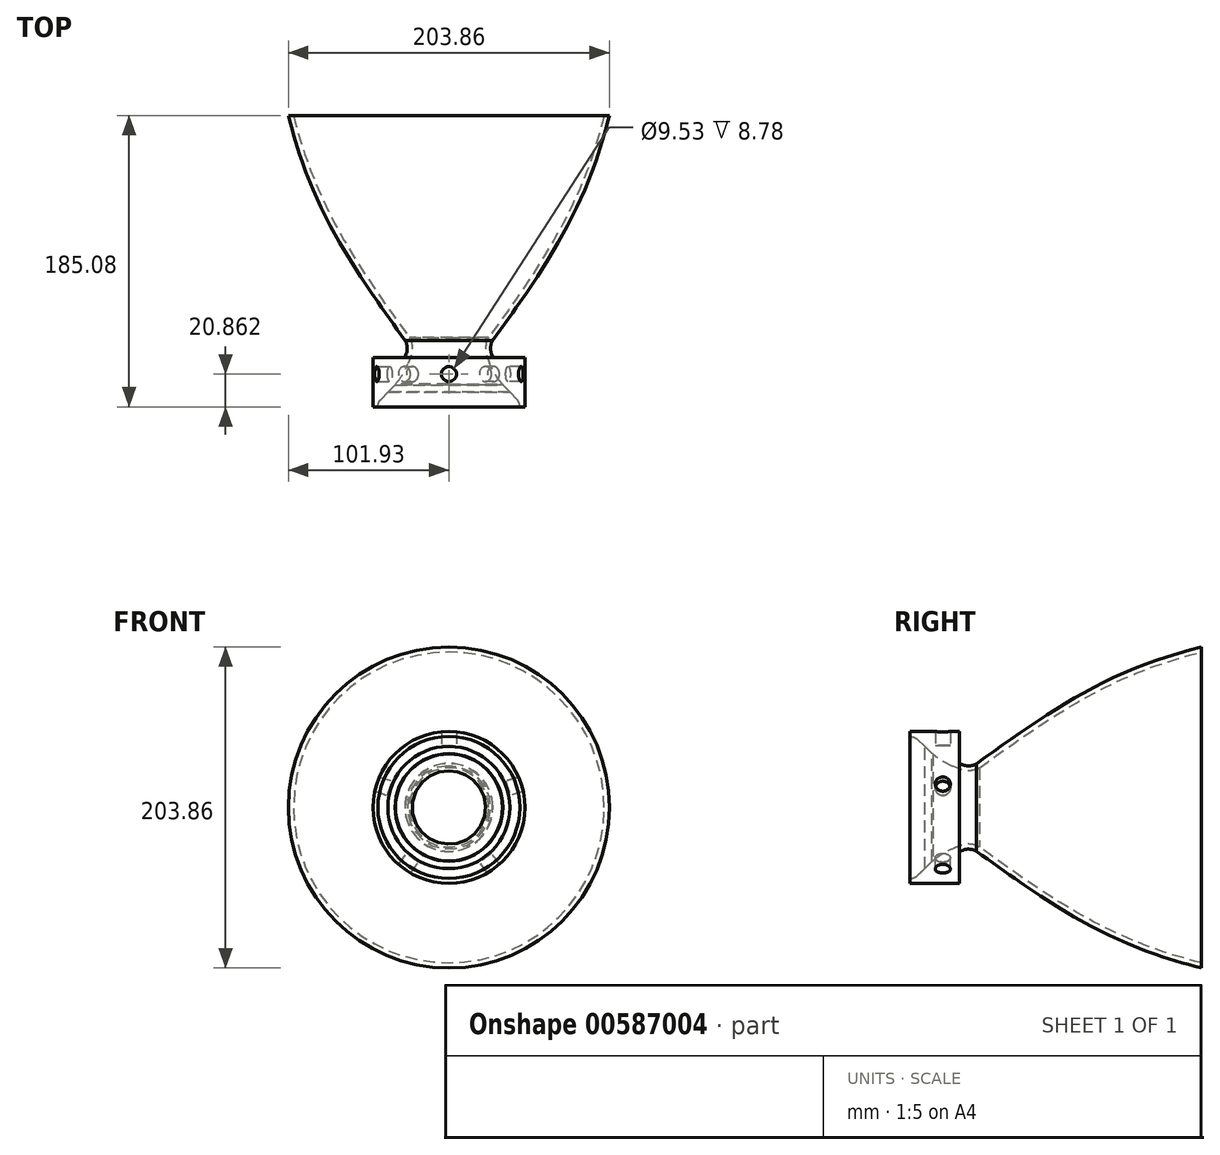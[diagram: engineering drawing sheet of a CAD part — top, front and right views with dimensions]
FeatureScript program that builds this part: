
annotation { "Feature Type Name" : "Feature", "Feature Type Description" : "" }
export const myFeature = defineFeature(function(context is Context, id is Id, definition is map)
    precondition{}
    {
        {
            var Q0;
            Q0=qCreatedBy(makeId("Right.planeOp"),FACE);
            var sketch = newSketch(context, id + "F0", { "sketchPlane" : qUnion([Q0])});
            skPoint(sketch, "E0", {"position": v(0, 25.4) * mm});
            skLineSegment(sketch, "E1", {"start": v(303.28, 127) * mm, "end": v(303.28, 0) * mm});
            skLineSegment(sketch, "E2", {"start": v(303.28, 0) * mm, "end": v(0, 0) * mm});
            skLineSegment(sketch, "E3", {"start": v(-31.1, 45.47) * mm, "end": v(-22.09, 36.92) * mm});
            skLineSegment(sketch, "E4", {"start": v(-9.32, 28.91) * mm, "end": v(-4.5, 27.1) * mm});
            skArc(sketch, "E5.filletArc", {"start": v(-4.5, 27.1) * mm, "mid": v(-0.09, 26.48) * mm, "end": v(4.17, 27.8) * mm});
            skPoint(sketch, "E6.visualSharp", {"position": v(-16.51, 31.63) * mm});
            skArc(sketch, "E6.filletArc", {"start": v(-22.09, 36.92) * mm, "mid": v(-16.1, 32.28) * mm, "end": v(-9.32, 28.91) * mm});
            skPoint(sketch, "E7.visualSharp", {"position": v(-34.05, 48.26) * mm});
            skArc(sketch, "E7.filletArc", {"start": v(-31.1, 45.47) * mm, "mid": v(-34.34, 47.54) * mm, "end": v(-38.1, 48.26) * mm});
            skFitSpline(sketch, "E8", {"points": [v(4.17, 27.8) * mm, v(117.26, 93.1) * mm, v(252.98, 119.48) * mm, v(303.28, 127) * mm], "startDerivative": vector(275.36, 198.38) * mm, "endDerivative": vector(183.33, 30.03) * mm});
            skLineSegment(sketch, "E9", {"start": v(-38.1, 48.26) * mm, "end": v(-38.1, 0) * mm});
            skLineSegment(sketch, "E10", {"start": v(-38.1, 0) * mm, "end": v(0, 0) * mm});
            skSolve(sketch);
        }
        {
            var Q0;
            Q0 = qSketchRegion(id + "F0", true);
            var Q1;
            Q1=sQuery(id+"F0.wireOp",EDGE,"E2");
            revolve(context, id + "F1", {"entities" : qUnion([Q0]), "axis" : qUnion([Q1]), "revolveType" : RevolveType.FULL});
        }
        {
            var Q0;
            Q0=makeQuery(id+"F1.opRevolve","SWEPT_FACE",FACE,{"disambiguationData":[OSD([sQuery(id+"F0.wireOp",EDGE,"E9")])]});
            cPlane(context, id + "F2", {"entities" : qUnion([Q0]), "cplaneType" : CPlaneType.OFFSET, "offset" : 27.18 * mm, "oppositeDirection" : true, "width" : 152.4 * mm, "height" : 152.4 * mm});
        }
        {
            var Q0;
            Q0=qCreatedBy(id+"F2.planeOp",FACE);
            var sketch = newSketch(context, id + "F3", { "sketchPlane" : qUnion([Q0])});
            skLineSegment(sketch, "E11.bottom", {"start": v(0, 61.38) * mm, "end": v(4.76, 61.38) * mm});
            skLineSegment(sketch, "E11.top", {"start": v(0, 33.85) * mm, "end": v(4.76, 33.85) * mm});
            skLineSegment(sketch, "E11.left", {"start": v(0, 61.38) * mm, "end": v(0, 33.85) * mm});
            skLineSegment(sketch, "E11.right", {"start": v(4.76, 61.38) * mm, "end": v(4.76, 33.85) * mm});
            skLineSegment(sketch, "E12.1.0", {"start": v(-58.37, 18.97) * mm, "end": v(-32.2, 10.46) * mm});
            skLineSegment(sketch, "E12.1.1", {"start": v(-56.9, 23.5) * mm, "end": v(-30.72, 15) * mm});
            skLineSegment(sketch, "E12.1.2", {"start": v(-58.37, 18.97) * mm, "end": v(-56.9, 23.5) * mm});
            skLineSegment(sketch, "E12.1.3", {"start": v(-32.2, 10.46) * mm, "end": v(-30.72, 15) * mm});
            skLineSegment(sketch, "E12.2.0", {"start": v(-36.08, -49.65) * mm, "end": v(-19.9, -27.39) * mm});
            skLineSegment(sketch, "E12.2.1", {"start": v(-39.93, -46.85) * mm, "end": v(-23.75, -24.59) * mm});
            skLineSegment(sketch, "E12.2.2", {"start": v(-36.08, -49.65) * mm, "end": v(-39.93, -46.85) * mm});
            skLineSegment(sketch, "E12.2.3", {"start": v(-19.9, -27.39) * mm, "end": v(-23.75, -24.59) * mm});
            skLineSegment(sketch, "E12.3.0", {"start": v(36.08, -49.65) * mm, "end": v(19.9, -27.39) * mm});
            skLineSegment(sketch, "E12.3.1", {"start": v(32.22, -52.45) * mm, "end": v(16.05, -30.19) * mm});
            skLineSegment(sketch, "E12.3.2", {"start": v(36.08, -49.65) * mm, "end": v(32.22, -52.45) * mm});
            skLineSegment(sketch, "E12.3.3", {"start": v(19.9, -27.39) * mm, "end": v(16.05, -30.19) * mm});
            skLineSegment(sketch, "E12.4.0", {"start": v(58.37, 18.97) * mm, "end": v(32.2, 10.46) * mm});
            skLineSegment(sketch, "E12.4.1", {"start": v(59.84, 14.44) * mm, "end": v(33.67, 5.93) * mm});
            skLineSegment(sketch, "E12.4.2", {"start": v(58.37, 18.97) * mm, "end": v(59.84, 14.44) * mm});
            skLineSegment(sketch, "E12.4.3", {"start": v(32.2, 10.46) * mm, "end": v(33.67, 5.93) * mm});
            skPoint(sketch, "E12.center", {"position": v(0, 0) * mm});
            skSolve(sketch);
        }
        {
            var Q0;
            Q0=makeQuery(id+"F3.imprint","IMPRINT",FACE,{"disambiguationData":[TD([[makeQuery(id+"F3.imprint","IMPRINT",EDGE,{"derivedFrom":sQuery(id+"F3.wireOp",EDGE,"E11.bottom")}),-1.0]])]});
            var Q1;
            Q1=sQuery(id+"F3.wireOp",EDGE,"E11.left");
            revolve(context, id + "F4", {"operationType" : NewBodyOperationType.REMOVE, "entities" : qUnion([Q0]), "axis" : qUnion([Q1]), "revolveType" : RevolveType.FULL, "oppositeDirection" : true});
        }
        {
            var Q0;
            Q0=makeQuery(id+"F3.imprint","IMPRINT",FACE,{"disambiguationData":[TD([[makeQuery(id+"F3.imprint","IMPRINT",EDGE,{"derivedFrom":sQuery(id+"F3.wireOp",EDGE,"E12.4.0")}),1.0]])]});
            var Q1;
            Q1=sQuery(id+"F3.wireOp",EDGE,"E12.4.0");
            revolve(context, id + "F5", {"operationType" : NewBodyOperationType.REMOVE, "entities" : qUnion([Q0]), "axis" : qUnion([Q1]), "revolveType" : RevolveType.FULL, "oppositeDirection" : true});
        }
        {
            var Q0;
            Q0=makeQuery(id+"F3.imprint","IMPRINT",FACE,{"disambiguationData":[TD([[makeQuery(id+"F3.imprint","IMPRINT",EDGE,{"derivedFrom":sQuery(id+"F3.wireOp",EDGE,"E12.3.0")}),1.0]])]});
            var Q1;
            Q1=sQuery(id+"F3.wireOp",EDGE,"E12.3.0");
            revolve(context, id + "F6", {"operationType" : NewBodyOperationType.REMOVE, "entities" : qUnion([Q0]), "axis" : qUnion([Q1]), "revolveType" : RevolveType.FULL});
        }
        {
            var Q0;
            Q0=makeQuery(id+"F3.imprint","IMPRINT",FACE,{"disambiguationData":[TD([[makeQuery(id+"F3.imprint","IMPRINT",EDGE,{"derivedFrom":sQuery(id+"F3.wireOp",EDGE,"E12.2.0")}),1.0]])]});
            var Q1;
            Q1=sQuery(id+"F3.wireOp",EDGE,"E12.2.0");
            revolve(context, id + "F7", {"operationType" : NewBodyOperationType.REMOVE, "entities" : qUnion([Q0]), "axis" : qUnion([Q1]), "revolveType" : RevolveType.FULL, "oppositeDirection" : true});
        }
        {
            var Q0;
            Q0=makeQuery(id+"F3.imprint","IMPRINT",FACE,{"disambiguationData":[TD([[makeQuery(id+"F3.imprint","IMPRINT",EDGE,{"derivedFrom":sQuery(id+"F3.wireOp",EDGE,"E12.1.0")}),1.0]])]});
            var Q1;
            Q1=sQuery(id+"F3.wireOp",EDGE,"E12.1.0");
            revolve(context, id + "F8", {"operationType" : NewBodyOperationType.REMOVE, "entities" : qUnion([Q0]), "axis" : qUnion([Q1]), "revolveType" : RevolveType.FULL});
        }
        {
            var Q0;
            Q0=makeQuery(id+"F1.opRevolve","SWEPT_FACE",FACE,{"disambiguationData":[OSD([sQuery(id+"F0.wireOp",EDGE,"E1")])]});
            var Q1;
            Q1=makeQuery(id+"F1.opRevolve","SWEPT_FACE",FACE,{"disambiguationData":[OSD([sQuery(id+"F0.wireOp",EDGE,"Ow1FXaBQ-uKWU-AUm1-Qf29-WGxy1pBPwJRH")])]});
            var Q2;
            Q2=makeQuery(id+"F1.opRevolve","SWEPT_FACE",FACE,{"disambiguationData":[OSD([sQuery(id+"F0.wireOp",EDGE,"E9")])]});
            shell(context, id + "F9", {"entities" : qUnion([Q0, Q1, Q2]), "thickness" : 3.17 * mm});
        }
        {
            var Q0;
            Q0=qCreatedBy(makeId("Right.planeOp"),FACE);
            var sketch = newSketch(context, id + "F10", { "sketchPlane" : qUnion([Q0])});
            skLineSegment(sketch, "E13.bottom", {"start": v(-146.71, 202.99) * mm, "end": v(438.5, 202.99) * mm});
            skLineSegment(sketch, "E13.top", {"start": v(-146.71, -194.5) * mm, "end": v(438.5, -194.5) * mm});
            skLineSegment(sketch, "E13.left", {"start": v(-146.71, 202.99) * mm, "end": v(-146.71, -194.5) * mm});
            skLineSegment(sketch, "E13.right", {"start": v(438.5, 202.99) * mm, "end": v(438.5, -194.5) * mm});
            skSolve(sketch);
        }
        {
            var Q0;
            Q0=qCreatedBy(makeId("Right.planeOp"),FACE);
            var sketch = newSketch(context, id + "F11", { "sketchPlane" : qUnion([Q0])});
            skArc(sketch, "E14.0", {"start": v(-38.1, 48.26) * mm, "mid": v(-34.34, 47.54) * mm, "end": v(-31.1, 45.47) * mm, "construction": true});
            skLineSegment(sketch, "E15", {"start": v(-38.1, 48.26) * mm, "end": v(-6.82, 48.26) * mm});
            skLineSegment(sketch, "E16", {"start": v(-6.82, 48.26) * mm, "end": v(-6.82, 26.64) * mm});
            skLineSegment(sketch, "E17", {"start": v(-6.82, 26.64) * mm, "end": v(-24.12, 34.21) * mm});
            skLineSegment(sketch, "E18", {"start": v(-24.12, 34.21) * mm, "end": v(-38.1, 48.26) * mm});
            skLineSegment(sketch, "E19", {"start": v(-117.34, 0) * mm, "end": v(111.52, 0) * mm, "construction": true});
            skSolve(sketch);
        }
        {
            var Q0;
            Q0=makeQuery(id+"F11.imprint","IMPRINT",FACE,{"disambiguationData":[TD([[makeQuery(id+"F11.imprint","IMPRINT",EDGE,{"derivedFrom":sQuery(id+"F11.wireOp",EDGE,"E15")}),-1.0]])]});
            var Q1;
            Q1=sQuery(id+"F11.wireOp",EDGE,"E19");
            revolve(context, id + "F12", {"operationType" : NewBodyOperationType.ADD, "entities" : qUnion([Q0]), "axis" : qUnion([Q1]), "revolveType" : RevolveType.FULL});
        }
        {
            var Q0;
            Q0=makeQuery(id+"F12.opRevolve","SWEPT_FACE",FACE,{"disambiguationData":[OSD([sQuery(id+"F11.wireOp",EDGE,"E16")])]});
            cPlane(context, id + "F13", {"entities" : qUnion([Q0]), "cplaneType" : CPlaneType.OFFSET, "offset" : 10.4 * mm, "oppositeDirection" : true, "width" : 152.4 * mm, "height" : 152.4 * mm});
        }
        {
            var Q0;
            Q0=qCreatedBy(id+"F13.planeOp",FACE);
            var sketch = newSketch(context, id + "F14", { "sketchPlane" : qUnion([Q0])});
            skLineSegment(sketch, "E20.bottom", {"start": v(0, 57.26) * mm, "end": v(-4.76, 57.26) * mm});
            skLineSegment(sketch, "E20.top", {"start": v(0, 39.48) * mm, "end": v(-4.76, 39.48) * mm});
            skLineSegment(sketch, "E20.left", {"start": v(0, 57.26) * mm, "end": v(0, 39.48) * mm});
            skLineSegment(sketch, "E20.right", {"start": v(-4.76, 57.26) * mm, "end": v(-4.76, 39.48) * mm});
            skLineSegment(sketch, "E21.1.0", {"start": v(-54.46, 17.7) * mm, "end": v(-37.55, 12.2) * mm});
            skLineSegment(sketch, "E21.1.1", {"start": v(-55.93, 13.17) * mm, "end": v(-39.02, 7.67) * mm});
            skLineSegment(sketch, "E21.1.2", {"start": v(-54.46, 17.7) * mm, "end": v(-55.93, 13.17) * mm});
            skLineSegment(sketch, "E21.1.3", {"start": v(-37.55, 12.2) * mm, "end": v(-39.02, 7.67) * mm});
            skLineSegment(sketch, "E21.2.0", {"start": v(-33.66, -46.33) * mm, "end": v(-23.2, -31.94) * mm});
            skLineSegment(sketch, "E21.2.1", {"start": v(-29.8, -49.12) * mm, "end": v(-19.35, -34.74) * mm});
            skLineSegment(sketch, "E21.2.2", {"start": v(-33.66, -46.33) * mm, "end": v(-29.8, -49.12) * mm});
            skLineSegment(sketch, "E21.2.3", {"start": v(-23.2, -31.94) * mm, "end": v(-19.35, -34.74) * mm});
            skLineSegment(sketch, "E21.3.0", {"start": v(33.66, -46.33) * mm, "end": v(23.2, -31.94) * mm});
            skLineSegment(sketch, "E21.3.1", {"start": v(37.51, -43.53) * mm, "end": v(27.06, -29.14) * mm});
            skLineSegment(sketch, "E21.3.2", {"start": v(33.66, -46.33) * mm, "end": v(37.51, -43.53) * mm});
            skLineSegment(sketch, "E21.3.3", {"start": v(23.2, -31.94) * mm, "end": v(27.06, -29.14) * mm});
            skLineSegment(sketch, "E21.4.0", {"start": v(54.46, 17.7) * mm, "end": v(37.55, 12.2) * mm});
            skLineSegment(sketch, "E21.4.1", {"start": v(52.99, 22.22) * mm, "end": v(36.08, 16.73) * mm});
            skLineSegment(sketch, "E21.4.2", {"start": v(54.46, 17.7) * mm, "end": v(52.99, 22.22) * mm});
            skLineSegment(sketch, "E21.4.3", {"start": v(37.55, 12.2) * mm, "end": v(36.08, 16.73) * mm});
            skPoint(sketch, "E21.center", {"position": v(0, 0) * mm});
            skSolve(sketch);
        }
        {
            var Q0;
            Q0=makeQuery(id+"F14.imprint","IMPRINT",FACE,{"disambiguationData":[TD([[makeQuery(id+"F14.imprint","IMPRINT",EDGE,{"derivedFrom":sQuery(id+"F14.wireOp",EDGE,"E20.bottom")}),1.0]])]});
            var Q1;
            Q1=sQuery(id+"F14.wireOp",EDGE,"E20.left");
            revolve(context, id + "F15", {"operationType" : NewBodyOperationType.REMOVE, "entities" : qUnion([Q0]), "axis" : qUnion([Q1]), "revolveType" : RevolveType.FULL, "oppositeDirection" : true});
        }
        {
            var Q0;
            Q0=makeQuery(id+"F14.imprint","IMPRINT",FACE,{"disambiguationData":[TD([[makeQuery(id+"F14.imprint","IMPRINT",EDGE,{"derivedFrom":sQuery(id+"F14.wireOp",EDGE,"E21.1.0")}),-1.0]])]});
            var Q1;
            Q1=sQuery(id+"F14.wireOp",EDGE,"E21.1.0");
            revolve(context, id + "F16", {"operationType" : NewBodyOperationType.REMOVE, "entities" : qUnion([Q0]), "axis" : qUnion([Q1]), "revolveType" : RevolveType.FULL, "oppositeDirection" : true});
        }
        {
            var Q0;
            Q0=makeQuery(id+"F14.imprint","IMPRINT",FACE,{"disambiguationData":[TD([[makeQuery(id+"F14.imprint","IMPRINT",EDGE,{"derivedFrom":sQuery(id+"F14.wireOp",EDGE,"E21.2.0")}),-1.0]])]});
            var Q1;
            Q1=sQuery(id+"F14.wireOp",EDGE,"E21.2.0");
            revolve(context, id + "F17", {"operationType" : NewBodyOperationType.REMOVE, "entities" : qUnion([Q0]), "axis" : qUnion([Q1]), "revolveType" : RevolveType.FULL, "oppositeDirection" : true});
        }
        {
            var Q0;
            Q0=makeQuery(id+"F14.imprint","IMPRINT",FACE,{"disambiguationData":[TD([[makeQuery(id+"F14.imprint","IMPRINT",EDGE,{"derivedFrom":sQuery(id+"F14.wireOp",EDGE,"E21.4.0")}),-1.0]])]});
            var Q1;
            Q1=sQuery(id+"F14.wireOp",EDGE,"E21.4.0");
            revolve(context, id + "F18", {"operationType" : NewBodyOperationType.REMOVE, "entities" : qUnion([Q0]), "axis" : qUnion([Q1]), "revolveType" : RevolveType.FULL, "oppositeDirection" : true});
        }
        {
            var Q0;
            Q0=makeQuery(id+"F14.imprint","IMPRINT",FACE,{"disambiguationData":[TD([[makeQuery(id+"F14.imprint","IMPRINT",EDGE,{"derivedFrom":sQuery(id+"F14.wireOp",EDGE,"E21.3.0")}),-1.0]])]});
            var Q1;
            Q1=sQuery(id+"F14.wireOp",EDGE,"E21.3.0");
            revolve(context, id + "F19", {"operationType" : NewBodyOperationType.REMOVE, "entities" : qUnion([Q0]), "axis" : qUnion([Q1]), "revolveType" : RevolveType.FULL, "oppositeDirection" : true});
        }
        {
            var Q0;
            Q0=qCreatedBy(makeId("Top.planeOp"),FACE);
            var sketch = newSketch(context, id + "F20", { "sketchPlane" : qUnion([Q0])});
            skLineSegment(sketch, "E22.bottom", {"start": v(-182.37, 146.98) * mm, "end": v(164.9, 146.98) * mm});
            skLineSegment(sketch, "E22.top", {"start": v(-182.37, 331.9) * mm, "end": v(164.9, 331.9) * mm});
            skLineSegment(sketch, "E22.left", {"start": v(-182.37, 146.98) * mm, "end": v(-182.37, 331.9) * mm});
            skLineSegment(sketch, "E22.right", {"start": v(164.9, 146.98) * mm, "end": v(164.9, 331.9) * mm});
            skSolve(sketch);
        }
        {
            var Q0;
            Q0 = qSketchRegion(id + "F20", true);
            extrude(context, id + "F21", {"entities" : qUnion([Q0]), "operationType" : NewBodyOperationType.REMOVE, "endBound" : BoundingType.SYMMETRIC, "oppositeDirection" : true, "depth" : 508 * mm, "offsetDistance" : 25.4 * mm});
        }
    });
